# Revit family: Hekatron_Feststellanlagen_SVG 522 TSK 03_DE_22.01
name_source: partatom
category: Brandmelder
revit_build: Autodesk Revit 2018 (Build: 20190510_1515(x64)
units: mm (PartAtom-declared; Revit-internal decimal feet)

## family parameters
Basisbauteil = Fläche
Beim Laden mit Abzugskörper schneiden = Nein
Bemaßung runder Anschluss = Durchmesser verwenden
Beschriftungsausrichtung beibehalten = Ja
Gemeinsam genutzt = Nein
OmniClass-Nummer = 23.85.30.21
OmniClass-Titel = Environmental Detection/Registration
Raumberechnungspunkt = Nein
Teiletyp = Normal

## types (1)
- SVG 522/TSK 03
    Bauartgenehmigungen = Z-6.500-2414, Z-6.500-2450, Z-6.500-2457
    Beschreibung = Feststellanlagensteuerung mit Netzgerät und Batteriepufferung für bahngebundene Förderanlagen, zur Steuerung von Decken- und Seitenklappen bei Schiebetoren und zum Einsatz in anderen Anwendungen.
    Betriebsspannung = 230 V AC
    Breite (mm) = 180.0
    Farbe = weiß, ähnlich RAL 9010
    Hersteller = Hekatron
    Höhe (mm) = 400.0
    Kabeleinführung = oben
    Link zu Ausschreibungstext = https://www.meinhplus.de
    Link zu Produktinformation = https://www.hekatron-planungstools.de
    Link zu ausschreiben.de = http://www.ausschreiben.de
    Link zum Datenblatt = https://www.hekatron-planungstools.de
    Material = Metall
    Modell = SVG 522/TSK 03
    Montageart = Aufputz
    Schutzart = IP 54
    Tiefe (mm) = 300.0
    Typenkommentare = Stromversorgungsgerät SVG 522 mit TSK 03
    UB A&S Artikel Nummer = 31-5400011-01-01
    URL = https://www.hekatron-brandschutz.de
    Version des BIM Objektes = 22.01
    Vorgabe-Ansicht = 1200 mm
    Zulässige Umgebungstemperatur = +5 °C bis +40 °C

## geometry (parser evidence)
native form markers: Sweep x2
no freeform markers — native parametric forms only
